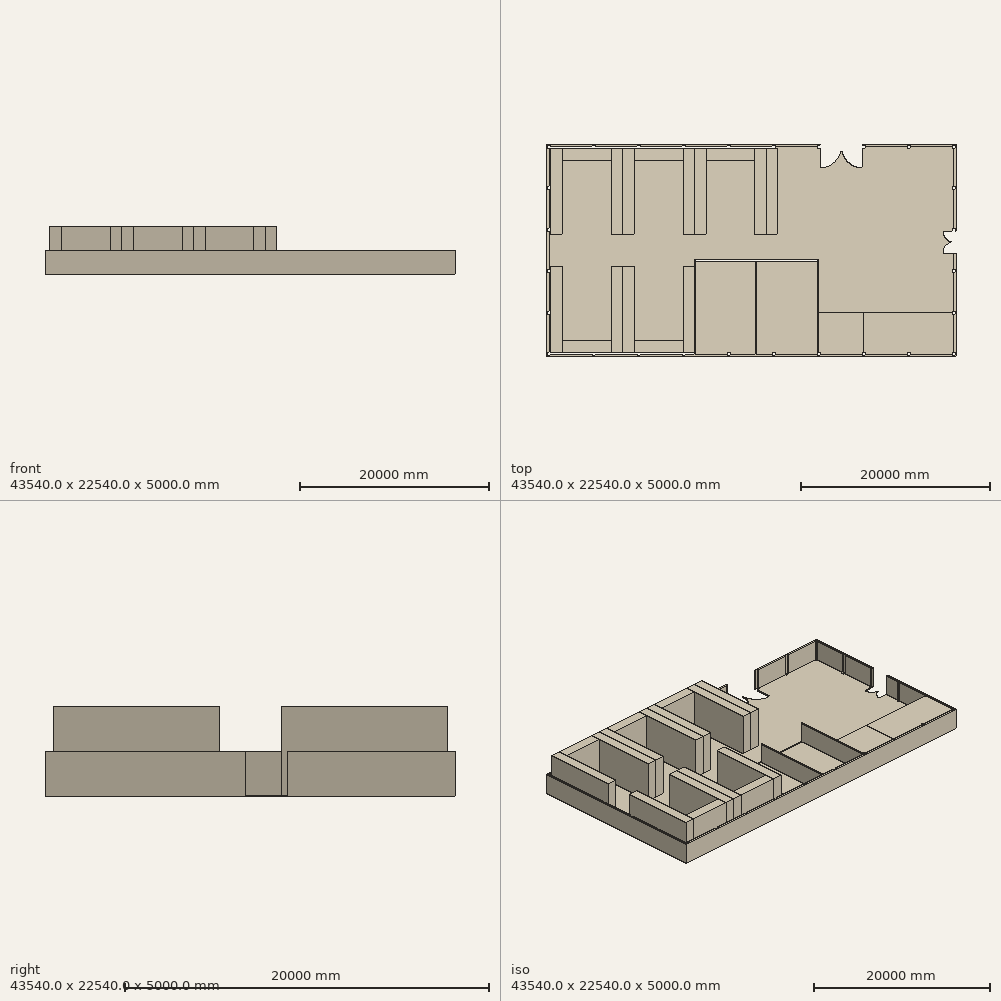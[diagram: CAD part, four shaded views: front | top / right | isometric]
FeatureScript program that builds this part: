
annotation { "Feature Type Name" : "Feature", "Feature Type Description" : "" }
export const myFeature = defineFeature(function(context is Context, id is Id, definition is map)
    precondition{}
    {
        {
            var Q0;
            Q0=qCreatedBy(makeId("Top.planeOp"),FACE);
            var sketch = newSketch(context, id + "F0", { "sketchPlane" : qUnion([Q0])});
            skLineSegment(sketch, "E0", {"start": v(0, 22000) * mm, "end": v(43000, 22000) * mm});
            skLineSegment(sketch, "E1", {"start": v(43000, 22000) * mm, "end": v(43000, 4400) * mm});
            skLineSegment(sketch, "E2", {"start": v(0, 22000) * mm, "end": v(0, 0) * mm});
            skLineSegment(sketch, "E3", {"start": v(0, 0) * mm, "end": v(28666.67, 0) * mm});
            skLineSegment(sketch, "E4.bottom", {"start": v(170, 22170) * mm, "end": v(-170, 22170) * mm});
            skLineSegment(sketch, "E4.top", {"start": v(170, 21830) * mm, "end": v(-170, 21830) * mm});
            skLineSegment(sketch, "E4.left", {"start": v(170, 22170) * mm, "end": v(170, 21830) * mm});
            skLineSegment(sketch, "E4.right", {"start": v(-170, 22170) * mm, "end": v(-170, 21830) * mm});
            skPoint(sketch, "E4.middle", {"position": v(0, 22000) * mm});
            skLineSegment(sketch, "E5.bottom", {"start": v(170, 170) * mm, "end": v(-170, 170) * mm});
            skLineSegment(sketch, "E5.top", {"start": v(170, -170) * mm, "end": v(-170, -170) * mm});
            skLineSegment(sketch, "E5.left", {"start": v(170, 170) * mm, "end": v(170, -170) * mm});
            skLineSegment(sketch, "E5.right", {"start": v(-170, 170) * mm, "end": v(-170, -170) * mm});
            skPoint(sketch, "E5.middle", {"position": v(0, 0) * mm});
            skLineSegment(sketch, "E6.0.1.0", {"start": v(170, 4230) * mm, "end": v(-170, 4230) * mm});
            skLineSegment(sketch, "E6.0.1.1", {"start": v(170, 4570) * mm, "end": v(-170, 4570) * mm});
            skLineSegment(sketch, "E6.0.1.2", {"start": v(170, 4570) * mm, "end": v(170, 4230) * mm});
            skLineSegment(sketch, "E6.0.1.3", {"start": v(-170, 4570) * mm, "end": v(-170, 4230) * mm});
            skLineSegment(sketch, "E6.0.2.0", {"start": v(170, 8630) * mm, "end": v(-170, 8630) * mm});
            skLineSegment(sketch, "E6.0.2.1", {"start": v(170, 8970) * mm, "end": v(-170, 8970) * mm});
            skLineSegment(sketch, "E6.0.2.2", {"start": v(170, 8970) * mm, "end": v(170, 8630) * mm});
            skLineSegment(sketch, "E6.0.2.3", {"start": v(-170, 8970) * mm, "end": v(-170, 8630) * mm});
            skLineSegment(sketch, "E6.0.3.0", {"start": v(170, 13030) * mm, "end": v(-170, 13030) * mm});
            skLineSegment(sketch, "E6.0.3.1", {"start": v(170, 13370) * mm, "end": v(-170, 13370) * mm});
            skLineSegment(sketch, "E6.0.3.2", {"start": v(170, 13370) * mm, "end": v(170, 13030) * mm});
            skLineSegment(sketch, "E6.0.3.3", {"start": v(-170, 13370) * mm, "end": v(-170, 13030) * mm});
            skLineSegment(sketch, "E6.0.4.0", {"start": v(170, 17430) * mm, "end": v(-170, 17430) * mm});
            skLineSegment(sketch, "E6.0.4.1", {"start": v(170, 17770) * mm, "end": v(-170, 17770) * mm});
            skLineSegment(sketch, "E6.0.4.2", {"start": v(170, 17770) * mm, "end": v(170, 17430) * mm});
            skLineSegment(sketch, "E6.0.4.3", {"start": v(-170, 17770) * mm, "end": v(-170, 17430) * mm});
            skLineSegment(sketch, "E7.0.1.0", {"start": v(43170, 4570) * mm, "end": v(43170, 4230) * mm});
            skPoint(sketch, "E7.0.1.1", {"position": v(43000, 4400) * mm});
            skLineSegment(sketch, "E7.0.1.2", {"start": v(42830, 4570) * mm, "end": v(42830, 4230) * mm});
            skLineSegment(sketch, "E7.0.1.4", {"start": v(43170, 4230) * mm, "end": v(42830, 4230) * mm});
            skLineSegment(sketch, "E7.0.1.5", {"start": v(43170, 4570) * mm, "end": v(42830, 4570) * mm});
            skLineSegment(sketch, "E7.0.2.0", {"start": v(43170, 8970) * mm, "end": v(43170, 8630) * mm});
            skPoint(sketch, "E7.0.2.1", {"position": v(43000, 8800) * mm});
            skLineSegment(sketch, "E7.0.2.2", {"start": v(42830, 8970) * mm, "end": v(42830, 8630) * mm});
            skLineSegment(sketch, "E7.0.2.4", {"start": v(43170, 8630) * mm, "end": v(42830, 8630) * mm});
            skLineSegment(sketch, "E7.0.2.5", {"start": v(43170, 8970) * mm, "end": v(42830, 8970) * mm});
            skLineSegment(sketch, "E7.0.3.0", {"start": v(43170, 13370) * mm, "end": v(43170, 13030) * mm});
            skPoint(sketch, "E7.0.3.1", {"position": v(43000, 13200) * mm});
            skLineSegment(sketch, "E7.0.3.2", {"start": v(42830, 13370) * mm, "end": v(42830, 13030) * mm});
            skLineSegment(sketch, "E7.0.3.4", {"start": v(43170, 13030) * mm, "end": v(42830, 13030) * mm});
            skLineSegment(sketch, "E7.0.3.5", {"start": v(43170, 13370) * mm, "end": v(42830, 13370) * mm});
            skLineSegment(sketch, "E7.0.4.0", {"start": v(43170, 17770) * mm, "end": v(43170, 17430) * mm});
            skPoint(sketch, "E7.0.4.1", {"position": v(43000, 17600) * mm});
            skLineSegment(sketch, "E7.0.4.2", {"start": v(42830, 17770) * mm, "end": v(42830, 17430) * mm});
            skLineSegment(sketch, "E7.0.4.4", {"start": v(43170, 17430) * mm, "end": v(42830, 17430) * mm});
            skLineSegment(sketch, "E7.0.4.5", {"start": v(43170, 17770) * mm, "end": v(42830, 17770) * mm});
            skPoint(sketch, "E8.1.0.0", {"position": v(4777.78, 22000) * mm});
            skLineSegment(sketch, "E8.1.0.1", {"start": v(4947.78, 22170) * mm, "end": v(4607.78, 22170) * mm});
            skLineSegment(sketch, "E8.1.0.2", {"start": v(4947.78, 22170) * mm, "end": v(4947.78, 21830) * mm});
            skLineSegment(sketch, "E8.1.0.3", {"start": v(4607.78, 22170) * mm, "end": v(4607.78, 21830) * mm});
            skLineSegment(sketch, "E8.1.0.4", {"start": v(4947.78, 21830) * mm, "end": v(4607.78, 21830) * mm});
            skPoint(sketch, "E8.2.0.0", {"position": v(9555.56, 22000) * mm});
            skLineSegment(sketch, "E8.2.0.1", {"start": v(9725.56, 22170) * mm, "end": v(9385.56, 22170) * mm});
            skLineSegment(sketch, "E8.2.0.2", {"start": v(9725.56, 22170) * mm, "end": v(9725.56, 21830) * mm});
            skLineSegment(sketch, "E8.2.0.3", {"start": v(9385.56, 22170) * mm, "end": v(9385.56, 21830) * mm});
            skLineSegment(sketch, "E8.2.0.4", {"start": v(9725.56, 21830) * mm, "end": v(9385.56, 21830) * mm});
            skPoint(sketch, "E8.3.0.0", {"position": v(14333.33, 22000) * mm});
            skLineSegment(sketch, "E8.3.0.1", {"start": v(14503.33, 22170) * mm, "end": v(14163.33, 22170) * mm});
            skLineSegment(sketch, "E8.3.0.2", {"start": v(14503.33, 22170) * mm, "end": v(14503.33, 21830) * mm});
            skLineSegment(sketch, "E8.3.0.3", {"start": v(14163.33, 22170) * mm, "end": v(14163.33, 21830) * mm});
            skLineSegment(sketch, "E8.3.0.4", {"start": v(14503.33, 21830) * mm, "end": v(14163.33, 21830) * mm});
            skPoint(sketch, "E8.4.0.0", {"position": v(19111.11, 22000) * mm});
            skLineSegment(sketch, "E8.4.0.1", {"start": v(19281.11, 22170) * mm, "end": v(18941.11, 22170) * mm});
            skLineSegment(sketch, "E8.4.0.2", {"start": v(19281.11, 22170) * mm, "end": v(19281.11, 21830) * mm});
            skLineSegment(sketch, "E8.4.0.3", {"start": v(18941.11, 22170) * mm, "end": v(18941.11, 21830) * mm});
            skLineSegment(sketch, "E8.4.0.4", {"start": v(19281.11, 21830) * mm, "end": v(18941.11, 21830) * mm});
            skPoint(sketch, "E8.5.0.0", {"position": v(23888.89, 22000) * mm});
            skLineSegment(sketch, "E8.5.0.1", {"start": v(24058.89, 22170) * mm, "end": v(23718.89, 22170) * mm});
            skLineSegment(sketch, "E8.5.0.2", {"start": v(24058.89, 22170) * mm, "end": v(24058.89, 21830) * mm});
            skLineSegment(sketch, "E8.5.0.3", {"start": v(23718.89, 22170) * mm, "end": v(23718.89, 21830) * mm});
            skLineSegment(sketch, "E8.5.0.4", {"start": v(24058.89, 21830) * mm, "end": v(23718.89, 21830) * mm});
            skPoint(sketch, "E8.6.0.0", {"position": v(28666.67, 22000) * mm});
            skLineSegment(sketch, "E8.6.0.1", {"start": v(28836.67, 22170) * mm, "end": v(28496.67, 22170) * mm});
            skLineSegment(sketch, "E8.6.0.2", {"start": v(28836.67, 22170) * mm, "end": v(28836.67, 21830) * mm});
            skLineSegment(sketch, "E8.6.0.3", {"start": v(28496.67, 22170) * mm, "end": v(28496.67, 21830) * mm});
            skLineSegment(sketch, "E8.6.0.4", {"start": v(28836.67, 21830) * mm, "end": v(28496.67, 21830) * mm});
            skPoint(sketch, "E8.7.0.0", {"position": v(33444.44, 22000) * mm});
            skLineSegment(sketch, "E8.7.0.1", {"start": v(33614.44, 22170) * mm, "end": v(33274.44, 22170) * mm});
            skLineSegment(sketch, "E8.7.0.2", {"start": v(33614.44, 22170) * mm, "end": v(33614.44, 21830) * mm});
            skLineSegment(sketch, "E8.7.0.3", {"start": v(33274.44, 22170) * mm, "end": v(33274.44, 21830) * mm});
            skLineSegment(sketch, "E8.7.0.4", {"start": v(33614.44, 21830) * mm, "end": v(33274.44, 21830) * mm});
            skPoint(sketch, "E8.8.0.0", {"position": v(38222.22, 22000) * mm});
            skLineSegment(sketch, "E8.8.0.1", {"start": v(38392.22, 22170) * mm, "end": v(38052.22, 22170) * mm});
            skLineSegment(sketch, "E8.8.0.2", {"start": v(38392.22, 22170) * mm, "end": v(38392.22, 21830) * mm});
            skLineSegment(sketch, "E8.8.0.3", {"start": v(38052.22, 22170) * mm, "end": v(38052.22, 21830) * mm});
            skLineSegment(sketch, "E8.8.0.4", {"start": v(38392.22, 21830) * mm, "end": v(38052.22, 21830) * mm});
            skPoint(sketch, "E8.9.0.0", {"position": v(43000, 22000) * mm});
            skLineSegment(sketch, "E8.9.0.1", {"start": v(43170, 22170) * mm, "end": v(42830, 22170) * mm});
            skLineSegment(sketch, "E8.9.0.2", {"start": v(43170, 22170) * mm, "end": v(43170, 21830) * mm});
            skLineSegment(sketch, "E8.9.0.3", {"start": v(42830, 22170) * mm, "end": v(42830, 21830) * mm});
            skLineSegment(sketch, "E8.9.0.4", {"start": v(43170, 21830) * mm, "end": v(42830, 21830) * mm});
            skLineSegment(sketch, "E9.1.0.0", {"start": v(4947.78, 170) * mm, "end": v(4607.78, 170) * mm});
            skLineSegment(sketch, "E9.1.0.1", {"start": v(4947.78, -170) * mm, "end": v(4607.78, -170) * mm});
            skPoint(sketch, "E9.1.0.2", {"position": v(4777.78, 0) * mm});
            skLineSegment(sketch, "E9.1.0.3", {"start": v(4607.78, 170) * mm, "end": v(4607.78, -170) * mm});
            skLineSegment(sketch, "E9.1.0.4", {"start": v(4947.78, 170) * mm, "end": v(4947.78, -170) * mm});
            skLineSegment(sketch, "E9.2.0.0", {"start": v(9725.56, 170) * mm, "end": v(9385.56, 170) * mm});
            skLineSegment(sketch, "E9.2.0.1", {"start": v(9725.56, -170) * mm, "end": v(9385.56, -170) * mm});
            skPoint(sketch, "E9.2.0.2", {"position": v(9555.56, 0) * mm});
            skLineSegment(sketch, "E9.2.0.3", {"start": v(9385.56, 170) * mm, "end": v(9385.56, -170) * mm});
            skLineSegment(sketch, "E9.2.0.4", {"start": v(9725.56, 170) * mm, "end": v(9725.56, -170) * mm});
            skLineSegment(sketch, "E9.3.0.0", {"start": v(14503.33, 170) * mm, "end": v(14163.33, 170) * mm});
            skLineSegment(sketch, "E9.3.0.1", {"start": v(14503.33, -170) * mm, "end": v(14163.33, -170) * mm});
            skPoint(sketch, "E9.3.0.2", {"position": v(14333.33, 0) * mm});
            skLineSegment(sketch, "E9.3.0.3", {"start": v(14163.33, 170) * mm, "end": v(14163.33, -170) * mm});
            skLineSegment(sketch, "E9.3.0.4", {"start": v(14503.33, 170) * mm, "end": v(14503.33, -170) * mm});
            skLineSegment(sketch, "E9.4.0.0", {"start": v(19281.11, 170) * mm, "end": v(18941.11, 170) * mm});
            skLineSegment(sketch, "E9.4.0.1", {"start": v(19281.11, -170) * mm, "end": v(18941.11, -170) * mm});
            skPoint(sketch, "E9.4.0.2", {"position": v(19111.11, 0) * mm});
            skLineSegment(sketch, "E9.4.0.3", {"start": v(18941.11, 170) * mm, "end": v(18941.11, -170) * mm});
            skLineSegment(sketch, "E9.4.0.4", {"start": v(19281.11, 170) * mm, "end": v(19281.11, -170) * mm});
            skLineSegment(sketch, "E9.5.0.0", {"start": v(24058.89, 170) * mm, "end": v(23718.89, 170) * mm});
            skLineSegment(sketch, "E9.5.0.1", {"start": v(24058.89, -170) * mm, "end": v(23718.89, -170) * mm});
            skPoint(sketch, "E9.5.0.2", {"position": v(23888.89, 0) * mm});
            skLineSegment(sketch, "E9.5.0.3", {"start": v(23718.89, 170) * mm, "end": v(23718.89, -170) * mm});
            skLineSegment(sketch, "E9.5.0.4", {"start": v(24058.89, 170) * mm, "end": v(24058.89, -170) * mm});
            skLineSegment(sketch, "E9.6.0.0", {"start": v(28836.67, 170) * mm, "end": v(28496.67, 170) * mm});
            skLineSegment(sketch, "E9.6.0.1", {"start": v(28836.67, -170) * mm, "end": v(28496.67, -170) * mm});
            skPoint(sketch, "E9.6.0.2", {"position": v(28666.67, 0) * mm});
            skLineSegment(sketch, "E9.6.0.3", {"start": v(28496.67, 170) * mm, "end": v(28496.67, -170) * mm});
            skLineSegment(sketch, "E9.6.0.4", {"start": v(28836.67, 170) * mm, "end": v(28836.67, -170) * mm});
            skLineSegment(sketch, "E9.7.0.0", {"start": v(33614.44, 170) * mm, "end": v(33274.44, 170) * mm});
            skLineSegment(sketch, "E9.7.0.1", {"start": v(33614.44, -170) * mm, "end": v(33274.44, -170) * mm});
            skPoint(sketch, "E9.7.0.2", {"position": v(33444.44, 0) * mm});
            skLineSegment(sketch, "E9.7.0.3", {"start": v(33274.44, 170) * mm, "end": v(33274.44, -170) * mm});
            skLineSegment(sketch, "E9.7.0.4", {"start": v(33614.44, 170) * mm, "end": v(33614.44, -170) * mm});
            skLineSegment(sketch, "E9.8.0.0", {"start": v(38392.22, 170) * mm, "end": v(38052.22, 170) * mm});
            skLineSegment(sketch, "E9.8.0.1", {"start": v(38392.22, -170) * mm, "end": v(38052.22, -170) * mm});
            skPoint(sketch, "E9.8.0.2", {"position": v(38222.22, 0) * mm});
            skLineSegment(sketch, "E9.8.0.3", {"start": v(38052.22, 170) * mm, "end": v(38052.22, -170) * mm});
            skLineSegment(sketch, "E9.8.0.4", {"start": v(38392.22, 170) * mm, "end": v(38392.22, -170) * mm});
            skLineSegment(sketch, "E9.9.0.0", {"start": v(43170, 170) * mm, "end": v(42830, 170) * mm});
            skLineSegment(sketch, "E9.9.0.1", {"start": v(43170, -170) * mm, "end": v(42830, -170) * mm});
            skPoint(sketch, "E9.9.0.2", {"position": v(43000, 0) * mm});
            skLineSegment(sketch, "E9.9.0.3", {"start": v(42830, 170) * mm, "end": v(42830, -170) * mm});
            skLineSegment(sketch, "E9.9.0.4", {"start": v(43170, 170) * mm, "end": v(43170, -170) * mm});
            skLineSegment(sketch, "E10.bottom", {"start": v(28836.67, 22000) * mm, "end": v(33274.44, 22000) * mm});
            skLineSegment(sketch, "E10.left", {"start": v(28836.67, 22000) * mm, "end": v(28836.67, 19781.11) * mm});
            skLineSegment(sketch, "E10.right", {"start": v(33274.44, 22000) * mm, "end": v(33274.44, 19781.11) * mm});
            skLineSegment(sketch, "E11", {"start": v(28666.67, 0) * mm, "end": v(43000, 0) * mm});
            skLineSegment(sketch, "E12", {"start": v(43000, 4400) * mm, "end": v(43000, 0) * mm});
            skLineSegment(sketch, "E13", {"start": v(43000, 4400) * mm, "end": v(28666.67, 4400) * mm});
            skLineSegment(sketch, "E14", {"start": v(28666.67, 4400) * mm, "end": v(28666.67, 0) * mm});
            skLineSegment(sketch, "E15", {"start": v(33444.44, 0) * mm, "end": v(33444.44, 4400) * mm});
            skLineSegment(sketch, "E16.top", {"start": v(43000, 10730) * mm, "end": v(41850, 10730) * mm});
            skLineSegment(sketch, "E16.left", {"start": v(43000, 13030) * mm, "end": v(43000, 10730) * mm});
            skLineSegment(sketch, "E17.top", {"start": v(69479.6, 14890.56) * mm, "end": v(70779.6, 14890.56) * mm});
            skLineSegment(sketch, "E17.left", {"start": v(69479.6, 17790.56) * mm, "end": v(69479.6, 14890.56) * mm});
            skLineSegment(sketch, "E17.right", {"start": v(70779.6, 17790.56) * mm, "end": v(70779.6, 14890.56) * mm});
            skLineSegment(sketch, "E18", {"start": v(69479.6, 17790.56) * mm, "end": v(69704.6, 17790.56) * mm});
            skLineSegment(sketch, "E19.MirrorCS", {"start": v(69904.6, 17790.56) * mm, "end": v(69904.6, 19390.56) * mm});
            skLineSegment(sketch, "E20", {"start": v(69704.6, 19390.56) * mm, "end": v(69704.6, 17790.56) * mm});
            skLineSegment(sketch, "E21.MirrorCS", {"start": v(70354.6, 17790.56) * mm, "end": v(70354.6, 19390.56) * mm});
            skLineSegment(sketch, "E22.MirrorCS", {"start": v(70554.6, 19390.56) * mm, "end": v(70554.6, 17790.56) * mm});
            skLineSegment(sketch, "E23", {"start": v(69704.6, 19390.56) * mm, "end": v(69904.6, 19390.56) * mm});
            skLineSegment(sketch, "E24.trimOffspring", {"start": v(70354.6, 19390.56) * mm, "end": v(70554.6, 19390.56) * mm});
            skLineSegment(sketch, "E25.bottom", {"start": v(64498.07, 14890.56) * mm, "end": v(65798.07, 14890.56) * mm});
            skLineSegment(sketch, "E25.top", {"start": v(64498.07, 19390.56) * mm, "end": v(65798.07, 19390.56) * mm});
            skLineSegment(sketch, "E25.left", {"start": v(64498.07, 14890.56) * mm, "end": v(64498.07, 19390.56) * mm});
            skLineSegment(sketch, "E25.right", {"start": v(65798.07, 14890.56) * mm, "end": v(65798.07, 19390.56) * mm});
            skLineSegment(sketch, "E26.trimOffspring", {"start": v(69904.6, 17790.56) * mm, "end": v(70354.6, 17790.56) * mm});
            skLineSegment(sketch, "E27.trimOffspring", {"start": v(70554.6, 17790.56) * mm, "end": v(70779.6, 17790.56) * mm});
            skLineSegment(sketch, "E28", {"start": v(30055.67, 19781.11) * mm, "end": v(30055.67, 12000) * mm});
            skLineSegment(sketch, "E29", {"start": v(30055.67, 12000) * mm, "end": v(0, 12000) * mm});
            skLineSegment(sketch, "E30", {"start": v(0, 10000) * mm, "end": v(32055.67, 10000) * mm});
            skLineSegment(sketch, "E31", {"start": v(32055.67, 10000) * mm, "end": v(32055.67, 19781.11) * mm});
            skLineSegment(sketch, "E32", {"start": v(31055.56, 19781.11) * mm, "end": v(31055.56, 11000) * mm, "construction": true});
            skLineSegment(sketch, "E33", {"start": v(31055.56, 11000) * mm, "end": v(0, 11000) * mm, "construction": true});
            skArc(sketch, "E34", {"start": v(43000, 11880) * mm, "mid": v(42186.83, 12216.83) * mm, "end": v(41850, 13030) * mm});
            skLineSegment(sketch, "E35", {"start": v(41850, 13030) * mm, "end": v(43000, 13030) * mm});
            skArc(sketch, "E36", {"start": v(43000, 11880) * mm, "mid": v(42186.83, 11543.17) * mm, "end": v(41850, 10730) * mm});
            skArc(sketch, "E37", {"start": v(31055.56, 22000) * mm, "mid": v(30405.66, 20431) * mm, "end": v(28836.67, 19781.11) * mm});
            skArc(sketch, "E38", {"start": v(31055.56, 22000) * mm, "mid": v(31705.45, 20431) * mm, "end": v(33274.44, 19781.11) * mm});
            skLineSegment(sketch, "E39", {"start": v(28836.67, 19781.11) * mm, "end": v(33274.44, 19781.11) * mm, "construction": true});
            skPoint(sketch, "E40", {"position": v(32055.67, 14890.56) * mm});
            skLineSegment(sketch, "E41.bottom", {"start": v(170, 21830) * mm, "end": v(1390, 21830) * mm});
            skLineSegment(sketch, "E41.top", {"start": v(170, 12730) * mm, "end": v(1390, 12730) * mm});
            skLineSegment(sketch, "E41.left", {"start": v(170, 21830) * mm, "end": v(170, 12730) * mm});
            skLineSegment(sketch, "E41.right", {"start": v(1390, 21830) * mm, "end": v(1390, 12730) * mm});
            skLineSegment(sketch, "E42.bottom", {"start": v(170, 9270) * mm, "end": v(1390, 9270) * mm});
            skLineSegment(sketch, "E42.top", {"start": v(170, 170) * mm, "end": v(1390, 170) * mm});
            skLineSegment(sketch, "E42.left", {"start": v(170, 9270) * mm, "end": v(170, 170) * mm});
            skLineSegment(sketch, "E42.right", {"start": v(1390, 9270) * mm, "end": v(1390, 170) * mm});
            skLineSegment(sketch, "E43.bottom", {"start": v(6590, 170) * mm, "end": v(7810, 170) * mm});
            skLineSegment(sketch, "E43.top", {"start": v(6590, 9270) * mm, "end": v(7810, 9270) * mm});
            skLineSegment(sketch, "E43.left", {"start": v(6590, 170) * mm, "end": v(6590, 9270) * mm});
            skLineSegment(sketch, "E43.right", {"start": v(7810, 170) * mm, "end": v(7810, 9270) * mm});
            skLineSegment(sketch, "E44.bottom", {"start": v(7810, 9270) * mm, "end": v(9030, 9270) * mm});
            skLineSegment(sketch, "E44.top", {"start": v(7810, 170) * mm, "end": v(9030, 170) * mm});
            skLineSegment(sketch, "E44.right", {"start": v(9030, 9270) * mm, "end": v(9030, 170) * mm});
            skLineSegment(sketch, "E45", {"start": v(28666.67, 4400) * mm, "end": v(28666.67, 10000) * mm});
            skLineSegment(sketch, "E46.1.0.0", {"start": v(6590, 21830) * mm, "end": v(7810, 21830) * mm});
            skLineSegment(sketch, "E46.1.0.1", {"start": v(7810, 21830) * mm, "end": v(7810, 12730) * mm});
            skLineSegment(sketch, "E46.1.0.2", {"start": v(6590, 12730) * mm, "end": v(7810, 12730) * mm});
            skLineSegment(sketch, "E46.1.0.3", {"start": v(6590, 21830) * mm, "end": v(6590, 12730) * mm});
            skLineSegment(sketch, "E47.bottom", {"start": v(7810, 21830) * mm, "end": v(9030, 21830) * mm});
            skLineSegment(sketch, "E47.top", {"start": v(7810, 12730) * mm, "end": v(9030, 12730) * mm});
            skLineSegment(sketch, "E47.right", {"start": v(9030, 21830) * mm, "end": v(9030, 12730) * mm});
            skLineSegment(sketch, "E48.bottom", {"start": v(1615.09, 17902.8) * mm, "end": v(6115.09, 17902.8) * mm});
            skLineSegment(sketch, "E48.top", {"start": v(1615.09, 16602.8) * mm, "end": v(6115.09, 16602.8) * mm});
            skLineSegment(sketch, "E48.left", {"start": v(1615.09, 17902.8) * mm, "end": v(1615.09, 16602.8) * mm});
            skLineSegment(sketch, "E48.right", {"start": v(6115.09, 17902.8) * mm, "end": v(6115.09, 16602.8) * mm});
            skLineSegment(sketch, "E49.1.0.0", {"start": v(14230, 21830) * mm, "end": v(15450, 21830) * mm});
            skLineSegment(sketch, "E49.1.0.1", {"start": v(15450, 21830) * mm, "end": v(16670, 21830) * mm});
            skLineSegment(sketch, "E49.1.0.2", {"start": v(14230, 21830) * mm, "end": v(14230, 12730) * mm});
            skLineSegment(sketch, "E49.1.0.3", {"start": v(15450, 21830) * mm, "end": v(15450, 12730) * mm});
            skLineSegment(sketch, "E49.1.0.4", {"start": v(16670, 21830) * mm, "end": v(16670, 12730) * mm});
            skLineSegment(sketch, "E49.1.0.5", {"start": v(14230, 12730) * mm, "end": v(15450, 12730) * mm});
            skLineSegment(sketch, "E49.1.0.6", {"start": v(15450, 12730) * mm, "end": v(16670, 12730) * mm});
            skLineSegment(sketch, "E49.2.0.0", {"start": v(21870, 21830) * mm, "end": v(23090, 21830) * mm});
            skLineSegment(sketch, "E49.2.0.1", {"start": v(23090, 21830) * mm, "end": v(24310, 21830) * mm});
            skLineSegment(sketch, "E49.2.0.2", {"start": v(21870, 21830) * mm, "end": v(21870, 12730) * mm});
            skLineSegment(sketch, "E49.2.0.3", {"start": v(23090, 21830) * mm, "end": v(23090, 12730) * mm});
            skLineSegment(sketch, "E49.2.0.4", {"start": v(24310, 21830) * mm, "end": v(24310, 12730) * mm});
            skLineSegment(sketch, "E49.2.0.5", {"start": v(21870, 12730) * mm, "end": v(23090, 12730) * mm});
            skLineSegment(sketch, "E49.2.0.6", {"start": v(23090, 12730) * mm, "end": v(24310, 12730) * mm});
            skLineSegment(sketch, "E49.direction1", {"start": v(6590, 21830) * mm, "end": v(14230, 21830) * mm, "construction": true});
            skLineSegment(sketch, "E50.1.0.1", {"start": v(14230, 170) * mm, "end": v(14230, 9270) * mm});
            skLineSegment(sketch, "E50.1.0.2", {"start": v(14230, 9270) * mm, "end": v(15450, 9270) * mm});
            skLineSegment(sketch, "E50.1.0.4", {"start": v(15450, 170) * mm, "end": v(15450, 9270) * mm});
            skLineSegment(sketch, "E50.1.0.6", {"start": v(14230, 170) * mm, "end": v(15450, 170) * mm});
            skLineSegment(sketch, "E50.direction1", {"start": v(6590, 170) * mm, "end": v(14230, 170) * mm, "construction": true});
            skLineSegment(sketch, "E51", {"start": v(15450, 0) * mm, "end": v(15450, 10000) * mm});
            skLineSegment(sketch, "E52", {"start": v(15450, 10000) * mm, "end": v(28666.67, 10000) * mm});
            skLineSegment(sketch, "E53", {"start": v(22058.33, 10000) * mm, "end": v(22058.33, 0) * mm});
            skLineSegment(sketch, "E54.bottom", {"start": v(1390, 21830) * mm, "end": v(6590, 21830) * mm});
            skLineSegment(sketch, "E54.top", {"start": v(1390, 20610) * mm, "end": v(6590, 20610) * mm});
            skLineSegment(sketch, "E54.left", {"start": v(1390, 21830) * mm, "end": v(1390, 20610) * mm});
            skLineSegment(sketch, "E54.right", {"start": v(6590, 21830) * mm, "end": v(6590, 20610) * mm});
            skLineSegment(sketch, "E55.bottom", {"start": v(9030, 21830) * mm, "end": v(14230, 21830) * mm});
            skLineSegment(sketch, "E55.top", {"start": v(9030, 20610) * mm, "end": v(14230, 20610) * mm});
            skLineSegment(sketch, "E55.left", {"start": v(9030, 21830) * mm, "end": v(9030, 20610) * mm});
            skLineSegment(sketch, "E55.right", {"start": v(14230, 21830) * mm, "end": v(14230, 20610) * mm});
            skLineSegment(sketch, "E56.bottom", {"start": v(16670, 21830) * mm, "end": v(21870, 21830) * mm});
            skLineSegment(sketch, "E56.top", {"start": v(16670, 20610) * mm, "end": v(21870, 20610) * mm});
            skLineSegment(sketch, "E56.left", {"start": v(16670, 21830) * mm, "end": v(16670, 20610) * mm});
            skLineSegment(sketch, "E56.right", {"start": v(21870, 21830) * mm, "end": v(21870, 20610) * mm});
            skLineSegment(sketch, "E57.bottom", {"start": v(1390, 170) * mm, "end": v(6590, 170) * mm});
            skLineSegment(sketch, "E57.top", {"start": v(1390, 1390) * mm, "end": v(6590, 1390) * mm});
            skLineSegment(sketch, "E57.left", {"start": v(1390, 170) * mm, "end": v(1390, 1390) * mm});
            skLineSegment(sketch, "E57.right", {"start": v(6590, 170) * mm, "end": v(6590, 1390) * mm});
            skLineSegment(sketch, "E58.bottom", {"start": v(9030, 170) * mm, "end": v(14230, 170) * mm});
            skLineSegment(sketch, "E58.top", {"start": v(9030, 1390) * mm, "end": v(14230, 1390) * mm});
            skLineSegment(sketch, "E58.left", {"start": v(9030, 170) * mm, "end": v(9030, 1390) * mm});
            skLineSegment(sketch, "E58.right", {"start": v(14230, 170) * mm, "end": v(14230, 1390) * mm});
            skLineSegment(sketch, "E59.0", {"start": v(28516.67, 4400) * mm, "end": v(28516.67, 0) * mm});
            skLineSegment(sketch, "E59.1", {"start": v(28516.67, 4400) * mm, "end": v(28516.67, 9850) * mm});
            skLineSegment(sketch, "E59.2", {"start": v(15600, 9850) * mm, "end": v(28516.67, 9850) * mm});
            skLineSegment(sketch, "E59.3", {"start": v(15600, 0) * mm, "end": v(15600, 9850) * mm});
            skLineSegment(sketch, "E60.0", {"start": v(21908.33, 10000) * mm, "end": v(21908.33, 0) * mm});
            skLineSegment(sketch, "E61", {"start": v(15600, 9850) * mm, "end": v(15600, 10000) * mm});
            skLineSegment(sketch, "E62", {"start": v(28516.67, 9850) * mm, "end": v(28516.67, 10000) * mm});
            skLineSegment(sketch, "E63.bottom", {"start": v(-270, 22270) * mm, "end": v(43270, 22270) * mm});
            skLineSegment(sketch, "E63.top", {"start": v(-270, -270) * mm, "end": v(43270, -270) * mm});
            skLineSegment(sketch, "E63.left", {"start": v(-270, 22270) * mm, "end": v(-270, -270) * mm});
            skLineSegment(sketch, "E63.right", {"start": v(43270, 22270) * mm, "end": v(43270, -270) * mm});
            skLineSegment(sketch, "E64", {"start": v(33274.44, 22170) * mm, "end": v(33274.44, 22270) * mm});
            skLineSegment(sketch, "E65", {"start": v(28836.67, 22170) * mm, "end": v(28836.67, 22270) * mm});
            skLineSegment(sketch, "E66", {"start": v(43170, 13030) * mm, "end": v(43270, 13030) * mm});
            skLineSegment(sketch, "E67", {"start": v(43000, 10730) * mm, "end": v(43270, 10730) * mm});
            skCircle(sketch, "E68", {"center": v(11620.8, 16888.07) * mm, "radius": 2342 * mm, "construction": true});
            skSolve(sketch);
        }
        {
            var Q0;
            {var subQ62=sQuery(id+"F0.wireOp",EDGE,"E7.0.2.2");Q0=makeQuery(id+"F0.imprint","IMPRINT",FACE,{"disambiguationData":[TD([[makeQuery(id+"F0.imprint","IMPRINT",EDGE,{"derivedFrom":subQ62}),-1.0]])]});}
            var Q1;
            Q1=makeQuery(id+"F0.imprint","IMPRINT",FACE,{"disambiguationData":[TD([[makeQuery(id+"F0.imprint","IMPRINT",EDGE,{"derivedFrom":sQuery(id+"F0.wireOp",EDGE,"E48.bottom")}),-1.0]])]});
            var Q2;
            {var subQ5=sQuery(id+"F0.wireOp",EDGE,"E42.bottom");Q2=makeQuery(id+"F0.imprint","IMPRINT",FACE,{"disambiguationData":[TD([[makeQuery(id+"F0.imprint","IMPRINT",EDGE,{"derivedFrom":subQ5}),1.0]])]});}
            var Q3;
            {var subQ7=sQuery(id+"F0.wireOp",EDGE,"E9.6.0.4");var subQ8=sQuery(id+"F0.wireOp",EDGE,"E9.6.0.0");var subQ9=makeQuery(id+"F0.imprint","INTERSECT",VERTEX,{"derivedFrom":[subQ8,subQ7]});Q3=makeQuery(id+"F0.imprint","IMPRINT",FACE,{"disambiguationData":[TD([[makeQuery(id+"F0.imprint","IMPRINT",EDGE,{"disambiguationData":[TD([[subQ9,-1.0]])],"derivedFrom":subQ8}),-1.0]])]});}
            var Q4;
            {var subQ18=sQuery(id+"F0.wireOp",EDGE,"E9.8.0.0");Q4=makeQuery(id+"F0.imprint","IMPRINT",FACE,{"disambiguationData":[TD([[makeQuery(id+"F0.imprint","IMPRINT",EDGE,{"derivedFrom":subQ18}),-1.0]])]});}
            var Q5;
            {var subQ11=sQuery(id+"F0.wireOp",EDGE,"E9.5.0.0");Q5=makeQuery(id+"F0.imprint","IMPRINT",FACE,{"disambiguationData":[TD([[makeQuery(id+"F0.imprint","IMPRINT",EDGE,{"derivedFrom":subQ11}),-1.0]])]});}
            var Q6;
            {var subQ1=sQuery(id+"F0.wireOp",EDGE,"E9.4.0.0");Q6=makeQuery(id+"F0.imprint","IMPRINT",FACE,{"disambiguationData":[TD([[makeQuery(id+"F0.imprint","IMPRINT",EDGE,{"derivedFrom":subQ1}),-1.0]])]});}
            extrude(context, id + "F1", {"entities" : qUnion([Q0, Q1, Q2, Q3, Q4, Q5, Q6]), "depth" : 100 * mm, "offsetDistance" : 25 * mm});
        }
        {
            var Q0;
            Q0=makeQuery(id+"F0.imprint","IMPRINT",FACE,{"disambiguationData":[TD([[makeQuery(id+"F0.imprint","IMPRINT",EDGE,{"derivedFrom":sQuery(id+"F0.wireOp",EDGE,"E46.1.0.0")}),-1.0]])]});
            var Q1;
            {var subQ3=sQuery(id+"F0.wireOp",EDGE,"E41.bottom");Q1=makeQuery(id+"F0.imprint","IMPRINT",FACE,{"disambiguationData":[TD([[makeQuery(id+"F0.imprint","IMPRINT",EDGE,{"derivedFrom":subQ3}),-1.0]])]});}
            var Q2;
            Q2=makeQuery(id+"F0.imprint","IMPRINT",FACE,{"disambiguationData":[TD([[makeQuery(id+"F0.imprint","IMPRINT",EDGE,{"derivedFrom":sQuery(id+"F0.wireOp",EDGE,"E49.1.0.2")}),1.0]])]});
            var Q3;
            Q3=makeQuery(id+"F0.imprint","IMPRINT",FACE,{"disambiguationData":[TD([[makeQuery(id+"F0.imprint","IMPRINT",EDGE,{"derivedFrom":sQuery(id+"F0.wireOp",EDGE,"E49.2.0.0")}),-1.0]])]});
            var Q4;
            {var subQ3=sQuery(id+"F0.wireOp",EDGE,"E42.bottom");Q4=makeQuery(id+"F0.imprint","IMPRINT",FACE,{"disambiguationData":[TD([[makeQuery(id+"F0.imprint","IMPRINT",EDGE,{"derivedFrom":subQ3}),-1.0]])]});}
            var Q5;
            Q5=makeQuery(id+"F0.imprint","IMPRINT",FACE,{"disambiguationData":[TD([[makeQuery(id+"F0.imprint","IMPRINT",EDGE,{"derivedFrom":sQuery(id+"F0.wireOp",EDGE,"E43.bottom")}),1.0]])]});
            var Q6;
            Q6=makeQuery(id+"F0.imprint","IMPRINT",FACE,{"disambiguationData":[TD([[makeQuery(id+"F0.imprint","IMPRINT",EDGE,{"derivedFrom":sQuery(id+"F0.wireOp",EDGE,"E50.1.0.1")}),-1.0]])]});
            extrude(context, id + "F2", {"entities" : qUnion([Q0, Q1, Q2, Q3, Q4, Q5, Q6]), "depth" : 5000 * mm, "offsetDistance" : 25 * mm});
        }
        {
            var Q0;
            Q0=makeQuery(id+"F0.imprint","IMPRINT",FACE,{"disambiguationData":[TD([[makeQuery(id+"F0.imprint","IMPRINT",EDGE,{"derivedFrom":sQuery(id+"F0.wireOp",EDGE,"E46.1.0.1")}),1.0]])]});
            var Q1;
            Q1=makeQuery(id+"F0.imprint","IMPRINT",FACE,{"disambiguationData":[TD([[makeQuery(id+"F0.imprint","IMPRINT",EDGE,{"derivedFrom":sQuery(id+"F0.wireOp",EDGE,"E49.1.0.1")}),-1.0]])]});
            var Q2;
            {var subQ0=sQuery(id+"F0.wireOp",EDGE,"E49.2.0.3");Q2=makeQuery(id+"F0.imprint","IMPRINT",FACE,{"disambiguationData":[TD([[makeQuery(id+"F0.imprint","IMPRINT",EDGE,{"derivedFrom":subQ0}),1.0]])]});}
            var Q3;
            Q3=makeQuery(id+"F0.imprint","IMPRINT",FACE,{"disambiguationData":[TD([[makeQuery(id+"F0.imprint","IMPRINT",EDGE,{"derivedFrom":sQuery(id+"F0.wireOp",EDGE,"E43.right")}),-1.0]])]});
            var Q4;
            {var subQ0=sQuery(id+"F0.wireOp",EDGE,"E50.1.0.0");Q4=makeQuery(id+"F0.imprint","IMPRINT",FACE,{"disambiguationData":[TD([[makeQuery(id+"F0.imprint","IMPRINT",EDGE,{"derivedFrom":subQ0}),1.0]])]});}
            extrude(context, id + "F3", {"entities" : qUnion([Q0, Q1, Q2, Q3, Q4]), "depth" : 5000 * mm, "offsetDistance" : 25 * mm});
        }
        {
            var Q0;
            Q0=makeQuery(id+"F0.imprint","IMPRINT",FACE,{"disambiguationData":[TD([[makeQuery(id+"F0.imprint","IMPRINT",EDGE,{"derivedFrom":sQuery(id+"F0.wireOp",EDGE,"E54.top")}),1.0]])]});
            var Q1;
            Q1=makeQuery(id+"F0.imprint","IMPRINT",FACE,{"disambiguationData":[TD([[makeQuery(id+"F0.imprint","IMPRINT",EDGE,{"derivedFrom":sQuery(id+"F0.wireOp",EDGE,"E55.top")}),1.0]])]});
            var Q2;
            Q2=makeQuery(id+"F0.imprint","IMPRINT",FACE,{"disambiguationData":[TD([[makeQuery(id+"F0.imprint","IMPRINT",EDGE,{"derivedFrom":sQuery(id+"F0.wireOp",EDGE,"E56.top")}),1.0]])]});
            var Q3;
            Q3=makeQuery(id+"F0.imprint","IMPRINT",FACE,{"disambiguationData":[TD([[makeQuery(id+"F0.imprint","IMPRINT",EDGE,{"derivedFrom":sQuery(id+"F0.wireOp",EDGE,"E57.top")}),-1.0]])]});
            var Q4;
            Q4=makeQuery(id+"F0.imprint","IMPRINT",FACE,{"disambiguationData":[TD([[makeQuery(id+"F0.imprint","IMPRINT",EDGE,{"derivedFrom":sQuery(id+"F0.wireOp",EDGE,"E58.top")}),-1.0]])]});
            extrude(context, id + "F4", {"entities" : qUnion([Q0, Q1, Q2, Q3, Q4]), "depth" : 5000 * mm, "offsetDistance" : 25 * mm});
        }
        {
            var Q0;
            {var subQ7=sQuery(id+"F0.wireOp",EDGE,"E59.3");Q0=makeQuery(id+"F0.imprint","IMPRINT",FACE,{"disambiguationData":[TD([[makeQuery(id+"F0.imprint","IMPRINT",EDGE,{"derivedFrom":subQ7}),1.0]])]});}
            var Q1;
            {var subQ0=sQuery(id+"F0.wireOp",EDGE,"E53");var subQ1=sQuery(id+"F0.wireOp",EDGE,"E3");var subQ2=makeQuery(id+"F0.imprint","INTERSECT",VERTEX,{"derivedFrom":[subQ1,subQ0]});Q1=makeQuery(id+"F0.imprint","IMPRINT",FACE,{"disambiguationData":[TD([[makeQuery(id+"F0.imprint","IMPRINT",EDGE,{"disambiguationData":[TD([[subQ2,1.0]])],"derivedFrom":subQ1}),1.0]])]});}
            var Q2;
            {var subQ0=sQuery(id+"F0.wireOp",EDGE,"E53");var subQ1=sQuery(id+"F0.wireOp",EDGE,"E52");var subQ2=makeQuery(id+"F0.imprint","INTERSECT",VERTEX,{"derivedFrom":[subQ1,subQ0]});Q2=makeQuery(id+"F0.imprint","IMPRINT",FACE,{"disambiguationData":[TD([[makeQuery(id+"F0.imprint","IMPRINT",EDGE,{"disambiguationData":[TD([[subQ2,1.0]])],"derivedFrom":subQ1}),-1.0]])]});}
            var Q3;
            {var subQ1=sQuery(id+"F0.wireOp",EDGE,"E45");Q3=makeQuery(id+"F0.imprint","IMPRINT",FACE,{"disambiguationData":[TD([[makeQuery(id+"F0.imprint","IMPRINT",EDGE,{"derivedFrom":subQ1}),1.0]])]});}
            extrude(context, id + "F5", {"entities" : qUnion([Q0, Q1, Q2, Q3]), "operationType" : NewBodyOperationType.ADD, "depth" : 2500 * mm, "offsetDistance" : 25 * mm});
        }
        {
            var Q0;
            {var subQ122=sQuery(id+"F0.wireOp",EDGE,"E4.bottom");Q0=makeQuery(id+"F0.imprint","IMPRINT",FACE,{"disambiguationData":[TD([[makeQuery(id+"F0.imprint","IMPRINT",EDGE,{"derivedFrom":subQ122}),-1.0]])]});}
            var Q1;
            {var subQ14=sQuery(id+"F0.wireOp",EDGE,"E7.0.3.0");Q1=makeQuery(id+"F0.imprint","IMPRINT",FACE,{"disambiguationData":[TD([[makeQuery(id+"F0.imprint","IMPRINT",EDGE,{"derivedFrom":subQ14}),1.0]])]});}
            extrude(context, id + "F6", {"entities" : qUnion([Q0, Q1]), "operationType" : NewBodyOperationType.ADD, "depth" : 2500 * mm, "offsetDistance" : 25 * mm});
        }
        {
            var Q0;
            {var subQ7=sQuery(id+"F0.wireOp",EDGE,"E9.6.0.4");var subQ8=sQuery(id+"F0.wireOp",EDGE,"E9.6.0.0");var subQ9=makeQuery(id+"F0.imprint","INTERSECT",VERTEX,{"derivedFrom":[subQ8,subQ7]});Q0=makeQuery(id+"F0.imprint","IMPRINT",FACE,{"disambiguationData":[TD([[makeQuery(id+"F0.imprint","IMPRINT",EDGE,{"disambiguationData":[TD([[subQ9,-1.0]])],"derivedFrom":subQ8}),-1.0]])]});}
            extrude(context, id + "F7", {"entities" : qUnion([Q0]), "depth" : 2500 * mm, "offsetDistance" : 25 * mm});
        }
        {
            var Q0;
            {var subQ11=sQuery(id+"F0.wireOp",EDGE,"E9.8.0.0");Q0=makeQuery(id+"F0.imprint","IMPRINT",FACE,{"disambiguationData":[TD([[makeQuery(id+"F0.imprint","IMPRINT",EDGE,{"derivedFrom":subQ11}),-1.0]])]});}
            extrude(context, id + "F8", {"entities" : qUnion([Q0]), "depth" : 2500 * mm, "offsetDistance" : 25 * mm});
        }
    });
